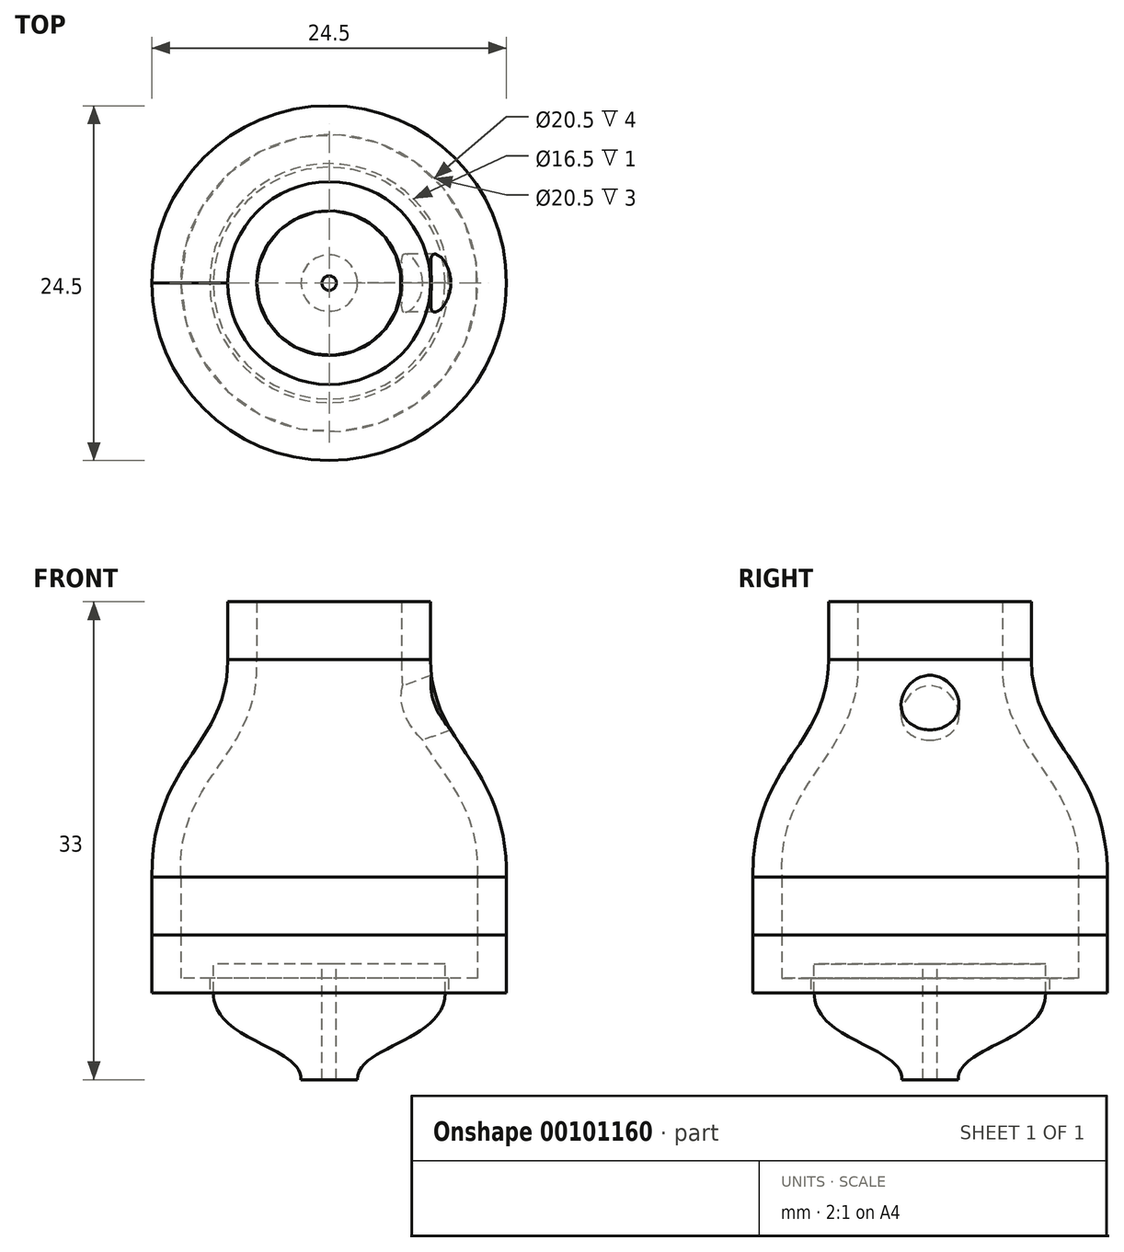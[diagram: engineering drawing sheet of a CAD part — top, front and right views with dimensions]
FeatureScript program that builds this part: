
annotation { "Feature Type Name" : "Feature", "Feature Type Description" : "" }
export const myFeature = defineFeature(function(context is Context, id is Id, definition is map)
    precondition{}
    {
        {
            var Q0;
            Q0=qCreatedBy(makeId("Top.planeOp"),FACE);
            var sketch = newSketch(context, id + "F0", { "sketchPlane" : qUnion([Q0])});
            skCircle(sketch, "E0", {"center": v(0, 0) * mm, "radius": 10.25 * mm});
            skCircle(sketch, "E1", {"center": v(0, 0) * mm, "radius": 8.25 * mm});
            skCircle(sketch, "E2", {"center": v(0, 0) * mm, "radius": 12.25 * mm});
            skCircle(sketch, "E3", {"center": v(0, 0) * mm, "radius": 8 * mm});
            skSolve(sketch);
        }
        {
            var Q0;
            Q0=makeQuery(id+"F0.imprint","IMPRINT",FACE,{"disambiguationData":[TD([[makeQuery(id+"F0.imprint","IMPRINT",EDGE,{"derivedFrom":sQuery(id+"F0.wireOp",EDGE,"E0")}),1.0]])]});
            extrude(context, id + "F1", {"entities" : qUnion([Q0]), "depth" : 1 * mm, "offsetDistance" : 25 * mm});
        }
        {
            var Q0;
            Q0=makeQuery(id+"F0.imprint","IMPRINT",FACE,{"disambiguationData":[TD([[makeQuery(id+"F0.imprint","IMPRINT",EDGE,{"derivedFrom":sQuery(id+"F0.wireOp",EDGE,"E0")}),-1.0]])]});
            extrude(context, id + "F2", {"entities" : qUnion([Q0]), "operationType" : NewBodyOperationType.ADD, "depth" : 4 * mm, "offsetDistance" : 25 * mm});
        }
        {
            var Q0;
            Q0=qCreatedBy(makeId("Front.planeOp"),FACE);
            var sketch = newSketch(context, id + "F3", { "sketchPlane" : qUnion([Q0])});
            skPoint(sketch, "E4", {"position": v(12.25, 4) * mm});
            skPoint(sketch, "E5", {"position": v(10.25, 4) * mm});
            skLineSegment(sketch, "E6", {"start": v(12.25, 4) * mm, "end": v(10.25, 4) * mm});
            skLineSegment(sketch, "E7", {"start": v(12.25, 4) * mm, "end": v(12.25, 8) * mm});
            skLineSegment(sketch, "E8", {"start": v(7, 27) * mm, "end": v(7, 23) * mm});
            skFitSpline(sketch, "E9", {"points": [v(12.25, 8) * mm, v(7, 23) * mm], "startDerivative": vector(0, 24) * mm, "endDerivative": vector(0, 18) * mm});
            skLineSegment(sketch, "E10", {"start": v(10.25, 4) * mm, "end": v(10.25, 8) * mm});
            skFitSpline(sketch, "E11.0", {"points": [v(10.25, 8) * mm, v(10.25, 8.9) * mm, v(10.1, 10.43) * mm, v(9.6, 12.22) * mm, v(8.87, 13.72) * mm, v(7.97, 15.14) * mm, v(6.96, 16.63) * mm, v(5.97, 18.35) * mm, v(5.2, 20.44) * mm, v(5, 22.1) * mm, v(5, 23) * mm]});
            skLineSegment(sketch, "E12", {"start": v(5, 23) * mm, "end": v(5, 27) * mm});
            skLineSegment(sketch, "E13", {"start": v(5, 27) * mm, "end": v(7, 27) * mm});
            skLineSegment(sketch, "E14", {"start": v(10.25, 4) * mm, "end": v(10.25, 3) * mm});
            skLineSegment(sketch, "E15", {"start": v(10.25, 3) * mm, "end": v(9.25, 3) * mm});
            skLineSegment(sketch, "E16", {"start": v(9.25, 3) * mm, "end": v(9.25, 12.9) * mm});
            skLineSegment(sketch, "E17", {"start": v(0, 0) * mm, "end": v(0, 27) * mm, "construction": true});
            skPoint(sketch, "E18", {"position": v(7.52, 19.96) * mm});
            skLineSegment(sketch, "E19", {"start": v(7.52, 19.96) * mm, "end": v(12.2, 21.68) * mm, "construction": true});
            skLineSegment(sketch, "E20", {"start": v(7.52, 19.96) * mm, "end": v(6.12, 23.8) * mm, "construction": true});
            skSolve(sketch);
        }
        {
            var Q0;
            {var subQ1=sQuery(id+"F3.wireOp",EDGE,"E10");Q0=makeQuery(id+"F3.imprint","IMPRINT",FACE,{"disambiguationData":[TD([[makeQuery(id+"F3.imprint","IMPRINT",EDGE,{"derivedFrom":subQ1}),1.0]])]});}
            var Q1;
            Q1=makeQuery(id+"F3.imprint","IMPRINT",FACE,{"disambiguationData":[TD([[makeQuery(id+"F3.imprint","IMPRINT",EDGE,{"derivedFrom":sQuery(id+"F3.wireOp",EDGE,"E6")}),-1.0]])]});
            var Q2;
            Q2=sQuery(id+"F3.wireOp",EDGE,"E17");
            revolve(context, id + "F4", {"surfaceOperationType" : NewSurfaceOperationType.NEW, "entities" : qUnion([Q0, Q1]), "axis" : qUnion([Q2]), "revolveType" : RevolveType.FULL});
        }
        {
            var Q0;
            Q0=sQuery(id+"F3.wireOp",EDGE,"E20");
            var Q1;
            Q1=sQuery(id+"F3.wireOp",VERTEX,"E8.start");
            cPlane(context, id + "F5", {"entities" : qUnion([Q0, Q1]), "cplaneType" : CPlaneType.LINE_ANGLE, "offset" : 25 * mm, "angle" : 90 * degree, "width" : 150 * mm, "height" : 150 * mm});
        }
        {
            var Q0;
            Q0=qCreatedBy(id+"F5.planeOp",FACE);
            var sketch = newSketch(context, id + "F6", { "sketchPlane" : qUnion([Q0])});
            skPoint(sketch, "E21.0", {"position": v(0, 16.15) * mm});
            skCircle(sketch, "E22", {"center": v(0, 16.15) * mm, "radius": 2 * mm});
            skSolve(sketch);
        }
        {
            var Q0;
            Q0=makeQuery(id+"F6.imprint","IMPRINT",FACE,{"disambiguationData":[TD([[makeQuery(id+"F6.imprint","IMPRINT",EDGE,{"derivedFrom":sQuery(id+"F6.wireOp",EDGE,"E22")}),1.0]])]});
            extrude(context, id + "F7", {"entities" : qUnion([Q0]), "operationType" : NewBodyOperationType.REMOVE, "oppositeDirection" : true, "depth" : 2 * mm, "offsetDistance" : 25 * mm, "hasSecondDirection" : true, "secondDirectionOppositeDirection" : false, "secondDirectionDepth" : 3.8 * mm});
        }
        {
            var Q0;
            Q0=qCreatedBy(makeId("Front.planeOp"),FACE);
            var sketch = newSketch(context, id + "F8", { "sketchPlane" : qUnion([Q0])});
            skLineSegment(sketch, "E23.0", {"start": v(-8, 0) * mm, "end": v(8, 0) * mm, "construction": true});
            skLineSegment(sketch, "E24", {"start": v(8, 0) * mm, "end": v(8, 2) * mm});
            skLineSegment(sketch, "E25", {"start": v(8, 2) * mm, "end": v(0, 2) * mm});
            skLineSegment(sketch, "E26", {"start": v(0, 2) * mm, "end": v(0, -6) * mm, "construction": true});
            skLineSegment(sketch, "E27", {"start": v(0, -6) * mm, "end": v(1.94, -6) * mm});
            skFitSpline(sketch, "E28", {"points": [v(8, 0) * mm, v(1.94, -6) * mm], "startDerivative": vector(0, -10.16) * mm, "endDerivative": vector(0, -7.16) * mm});
            skLineSegment(sketch, "E29", {"start": v(0.5, 2) * mm, "end": v(0.5, -6) * mm});
            skSolve(sketch);
        }
        {
            var Q0;
            Q0=makeQuery(id+"F8.imprint","IMPRINT",FACE,{"disambiguationData":[TD([[makeQuery(id+"F8.imprint","IMPRINT",EDGE,{"derivedFrom":sQuery(id+"F8.wireOp",EDGE,"E24")}),1.0]])]});
            var Q1;
            Q1=sQuery(id+"F8.wireOp",EDGE,"E26");
            revolve(context, id + "F9", {"surfaceOperationType" : NewSurfaceOperationType.NEW, "entities" : qUnion([Q0]), "axis" : qUnion([Q1]), "revolveType" : RevolveType.FULL});
        }
    });
